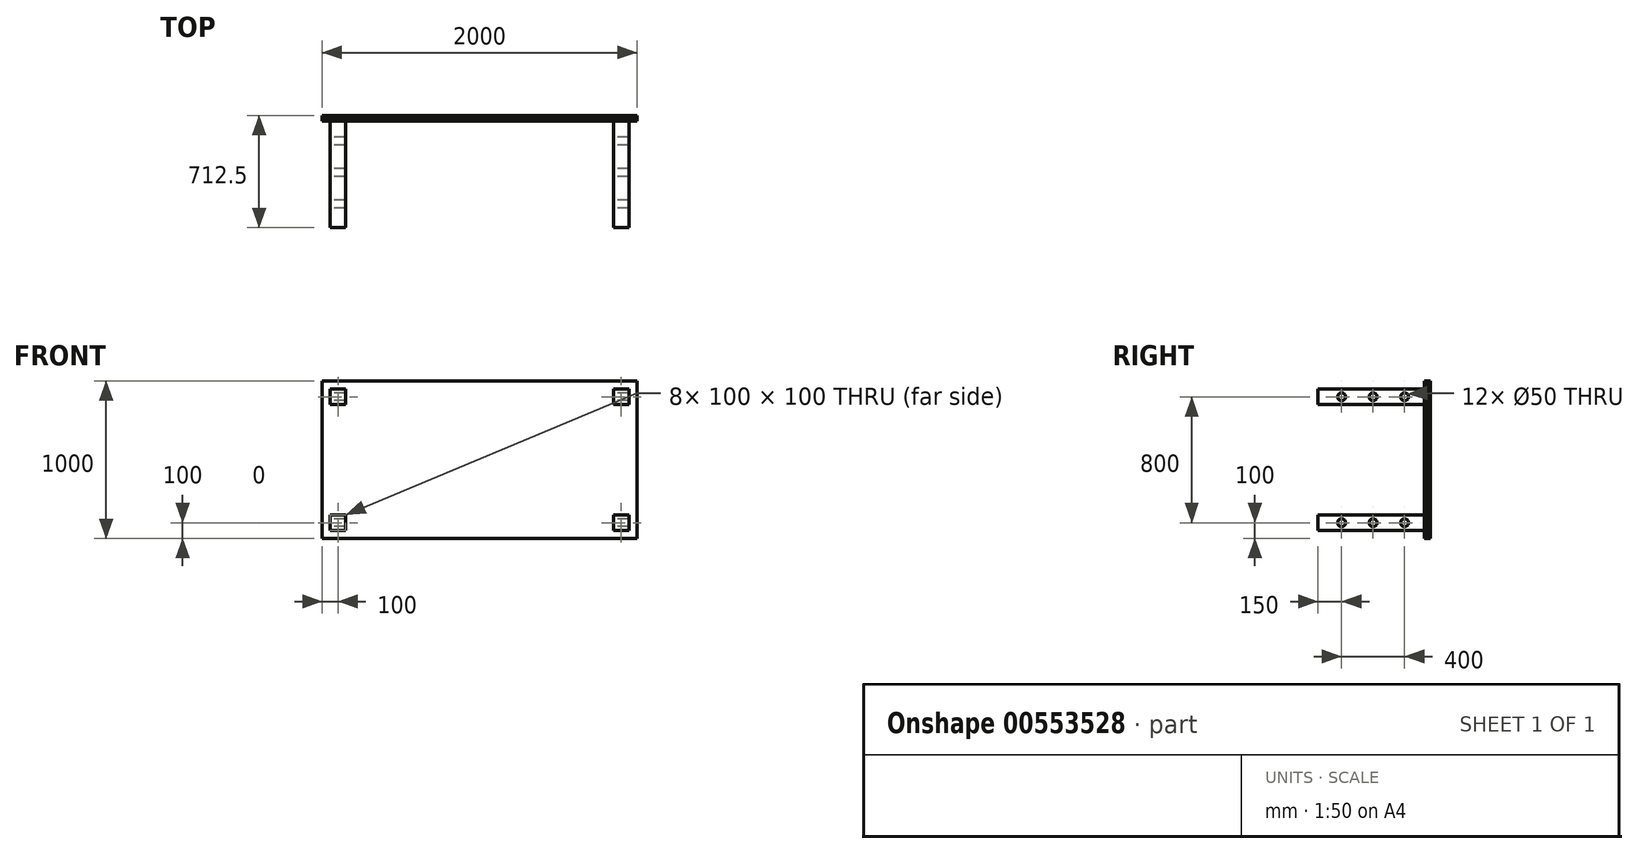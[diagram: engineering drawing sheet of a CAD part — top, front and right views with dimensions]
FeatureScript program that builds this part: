
annotation { "Feature Type Name" : "Feature", "Feature Type Description" : "" }
export const myFeature = defineFeature(function(context is Context, id is Id, definition is map)
    precondition{}
    {
        {
            var Q0;
            Q0=qCreatedBy(makeId("Front.planeOp"),FACE);
            var sketch = newSketch(context, id + "F0", { "sketchPlane" : qUnion([Q0])});
            skLineSegment(sketch, "E0.bottom", {"start": v(-50, 950) * mm, "end": v(1950, 950) * mm});
            skLineSegment(sketch, "E0.top", {"start": v(-50, -50) * mm, "end": v(1950, -50) * mm});
            skLineSegment(sketch, "E0.left", {"start": v(-50, 950) * mm, "end": v(-50, -50) * mm});
            skLineSegment(sketch, "E0.right", {"start": v(1950, 950) * mm, "end": v(1950, -50) * mm});
            skLineSegment(sketch, "E1.bottom", {"start": v(0, 900) * mm, "end": v(100, 900) * mm});
            skLineSegment(sketch, "E1.top", {"start": v(0, 800) * mm, "end": v(100, 800) * mm});
            skLineSegment(sketch, "E1.left", {"start": v(0, 900) * mm, "end": v(0, 800) * mm});
            skLineSegment(sketch, "E1.right", {"start": v(100, 900) * mm, "end": v(100, 800) * mm});
            skLineSegment(sketch, "E2.bottom", {"start": v(1800, 900) * mm, "end": v(1900, 900) * mm});
            skLineSegment(sketch, "E2.top", {"start": v(1800, 800) * mm, "end": v(1900, 800) * mm});
            skLineSegment(sketch, "E2.left", {"start": v(1800, 900) * mm, "end": v(1800, 800) * mm});
            skLineSegment(sketch, "E2.right", {"start": v(1900, 900) * mm, "end": v(1900, 800) * mm});
            skLineSegment(sketch, "E3.bottom", {"start": v(0, 100) * mm, "end": v(100, 100) * mm});
            skLineSegment(sketch, "E3.top", {"start": v(0, 0) * mm, "end": v(100, 0) * mm});
            skLineSegment(sketch, "E3.left", {"start": v(0, 100) * mm, "end": v(0, 0) * mm});
            skLineSegment(sketch, "E3.right", {"start": v(100, 100) * mm, "end": v(100, 0) * mm});
            skLineSegment(sketch, "E4.bottom", {"start": v(1800, 100) * mm, "end": v(1900, 100) * mm});
            skLineSegment(sketch, "E4.top", {"start": v(1800, 0) * mm, "end": v(1900, 0) * mm});
            skLineSegment(sketch, "E4.left", {"start": v(1800, 100) * mm, "end": v(1800, 0) * mm});
            skLineSegment(sketch, "E4.right", {"start": v(1900, 100) * mm, "end": v(1900, 0) * mm});
            skSolve(sketch);
        }
        {
            var Q0;
            Q0=makeQuery(id+"F0.imprint","IMPRINT",FACE,{"disambiguationData":[TD([[makeQuery(id+"F0.imprint","IMPRINT",EDGE,{"derivedFrom":sQuery(id+"F0.wireOp",EDGE,"E0.bottom")}),-1.0]])]});
            extrude(context, id + "F1", {"entities" : qUnion([Q0]), "endBound" : BoundingType.SYMMETRIC, "depth" : 25 * mm, "offsetDistance" : 25 * mm});
        }
        {
            var Q0;
            Q0=makeQuery(id+"F0.imprint","IMPRINT",FACE,{"disambiguationData":[TD([[makeQuery(id+"F0.imprint","IMPRINT",EDGE,{"derivedFrom":sQuery(id+"F0.wireOp",EDGE,"E1.bottom")}),-1.0]])]});
            var Q1;
            Q1=makeQuery(id+"F0.imprint","IMPRINT",FACE,{"disambiguationData":[TD([[makeQuery(id+"F0.imprint","IMPRINT",EDGE,{"derivedFrom":sQuery(id+"F0.wireOp",EDGE,"E2.bottom")}),-1.0]])]});
            var Q2;
            Q2=makeQuery(id+"F0.imprint","IMPRINT",FACE,{"disambiguationData":[TD([[makeQuery(id+"F0.imprint","IMPRINT",EDGE,{"derivedFrom":sQuery(id+"F0.wireOp",EDGE,"E4.bottom")}),-1.0]])]});
            var Q3;
            Q3=makeQuery(id+"F0.imprint","IMPRINT",FACE,{"disambiguationData":[TD([[makeQuery(id+"F0.imprint","IMPRINT",EDGE,{"derivedFrom":sQuery(id+"F0.wireOp",EDGE,"E3.bottom")}),-1.0]])]});
            extrude(context, id + "F2", {"entities" : qUnion([Q0, Q1, Q2, Q3]), "depth" : 700 * mm, "offsetDistance" : 25 * mm});
        }
        {
            var Q0;
            Q0=makeQuery(id+"F0.imprint","IMPRINT",FACE,{"disambiguationData":[TD([[makeQuery(id+"F0.imprint","IMPRINT",EDGE,{"derivedFrom":sQuery(id+"F0.wireOp",EDGE,"E0.bottom")}),-1.0]])]});
            extrude(context, id + "F3", {"entities" : qUnion([Q0]), "depth" : 25 * mm, "offsetDistance" : 25 * mm});
        }
        {
            var Q0;
            Q0=makeQuery(id+"F2.opExtrude","SWEPT_FACE",FACE,{"disambiguationData":[OSD([sQuery(id+"F0.wireOp",EDGE,"E3.left")])]});
            var sketch = newSketch(context, id + "F4", { "sketchPlane" : qUnion([Q0])});
            skCircle(sketch, "E5", {"center": v(150, 50) * mm, "radius": 25 * mm});
            skCircle(sketch, "E6", {"center": v(350, 50) * mm, "radius": 25 * mm});
            skCircle(sketch, "E7", {"center": v(550, 50) * mm, "radius": 25 * mm});
            skCircle(sketch, "E8", {"center": v(150, 850) * mm, "radius": 25 * mm});
            skCircle(sketch, "E9", {"center": v(350, 850) * mm, "radius": 25 * mm});
            skCircle(sketch, "E10", {"center": v(550, 850) * mm, "radius": 25 * mm});
            skSolve(sketch);
        }
        {
            var Q0;
            Q0=makeQuery(id+"F4.imprint","IMPRINT",FACE,{"disambiguationData":[TD([[makeQuery(id+"F4.imprint","IMPRINT",EDGE,{"derivedFrom":sQuery(id+"F4.wireOp",EDGE,"E8")}),1.0]])]});
            var Q1;
            Q1=makeQuery(id+"F4.imprint","IMPRINT",FACE,{"disambiguationData":[TD([[makeQuery(id+"F4.imprint","IMPRINT",EDGE,{"derivedFrom":sQuery(id+"F4.wireOp",EDGE,"E6")}),1.0]])]});
            var Q2;
            Q2=makeQuery(id+"F4.imprint","IMPRINT",FACE,{"disambiguationData":[TD([[makeQuery(id+"F4.imprint","IMPRINT",EDGE,{"derivedFrom":sQuery(id+"F4.wireOp",EDGE,"E7")}),1.0]])]});
            var Q3;
            Q3=makeQuery(id+"F4.imprint","IMPRINT",FACE,{"disambiguationData":[TD([[makeQuery(id+"F4.imprint","IMPRINT",EDGE,{"derivedFrom":sQuery(id+"F4.wireOp",EDGE,"E9")}),1.0]])]});
            var Q4;
            Q4=makeQuery(id+"F4.imprint","IMPRINT",FACE,{"disambiguationData":[TD([[makeQuery(id+"F4.imprint","IMPRINT",EDGE,{"derivedFrom":sQuery(id+"F4.wireOp",EDGE,"E10")}),1.0]])]});
            var Q5;
            Q5=makeQuery(id+"F4.imprint","IMPRINT",FACE,{"disambiguationData":[TD([[makeQuery(id+"F4.imprint","IMPRINT",EDGE,{"derivedFrom":sQuery(id+"F4.wireOp",EDGE,"E5")}),1.0]])]});
            extrude(context, id + "F5", {"entities" : qUnion([Q0, Q1, Q2, Q3, Q4, Q5]), "operationType" : NewBodyOperationType.REMOVE, "endBound" : BoundingType.THROUGH_ALL, "oppositeDirection" : true, "depth" : 25 * mm, "offsetDistance" : 25 * mm});
        }
    });
